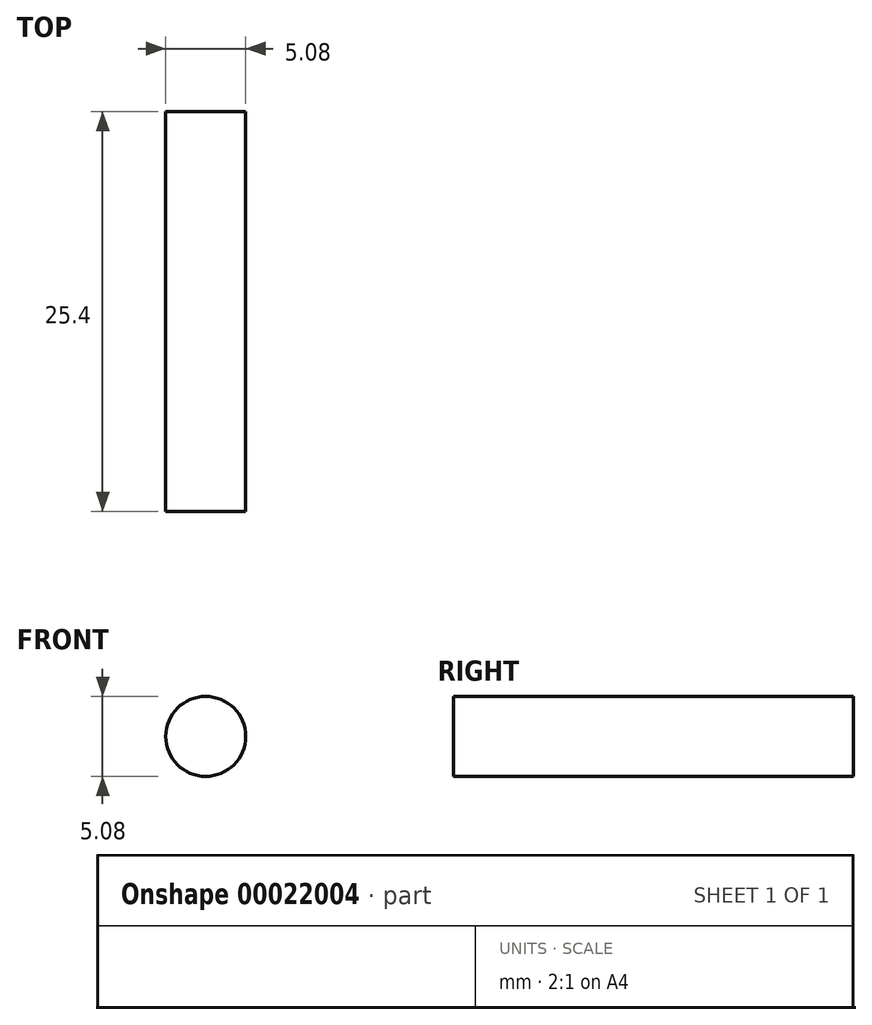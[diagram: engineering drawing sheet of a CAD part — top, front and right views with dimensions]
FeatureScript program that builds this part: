
annotation { "Feature Type Name" : "Feature", "Feature Type Description" : "" }
export const myFeature = defineFeature(function(context is Context, id is Id, definition is map)
    precondition{}
    {
        {
            var Q0;
            Q0=qCreatedBy(makeId("Front.planeOp"),FACE);
            var sketch = newSketch(context, id + "F0", { "sketchPlane" : qUnion([Q0])});
            skCircle(sketch, "E0", {"center": v(0, 0) * mm, "radius": 2.54 * mm});
            skSolve(sketch);
        }
        {
            var Q0;
            Q0 = qSketchRegion(id + "F0", true);
            extrude(context, id + "F1", {"entities" : qUnion([Q0]), "depth" : 25.4 * mm});
        }
    });
